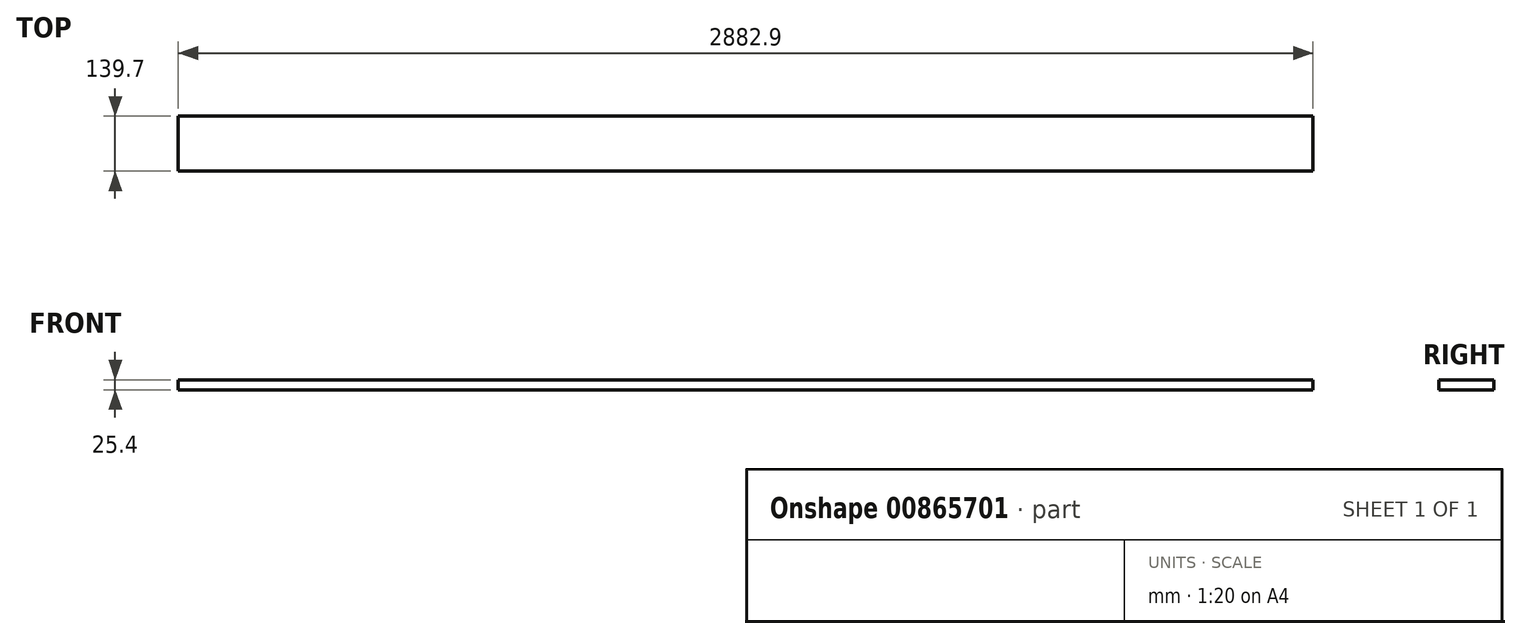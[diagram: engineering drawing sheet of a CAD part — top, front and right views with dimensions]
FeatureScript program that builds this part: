
annotation { "Feature Type Name" : "Feature", "Feature Type Description" : "" }
export const myFeature = defineFeature(function(context is Context, id is Id, definition is map)
    precondition{}
    {
        {
            var Q0;
            Q0=qCreatedBy(makeId("Right.planeOp"),FACE);
            var sketch = newSketch(context, id + "F0", { "sketchPlane" : qUnion([Q0])});
            skLineSegment(sketch, "E0.bottom", {"start": v(0, 0) * mm, "end": v(139.7, 0) * mm});
            skLineSegment(sketch, "E0.top", {"start": v(0, 25.4) * mm, "end": v(139.7, 25.4) * mm});
            skLineSegment(sketch, "E0.left", {"start": v(0, 0) * mm, "end": v(0, 25.4) * mm});
            skLineSegment(sketch, "E0.right", {"start": v(139.7, 0) * mm, "end": v(139.7, 25.4) * mm});
            skSolve(sketch);
        }
        {
            var Q0;
            Q0=makeQuery(id+"F0.imprint","IMPRINT",FACE,{"disambiguationData":[TD([[makeQuery(id+"F0.imprint","IMPRINT",EDGE,{"derivedFrom":sQuery(id+"F0.wireOp",EDGE,"E0.bottom")}),1.0]])]});
            extrude(context, id + "F1", {"entities" : qUnion([Q0]), "depth" : 2882.9 * mm, "offsetDistance" : 25.4 * mm});
        }
    });
